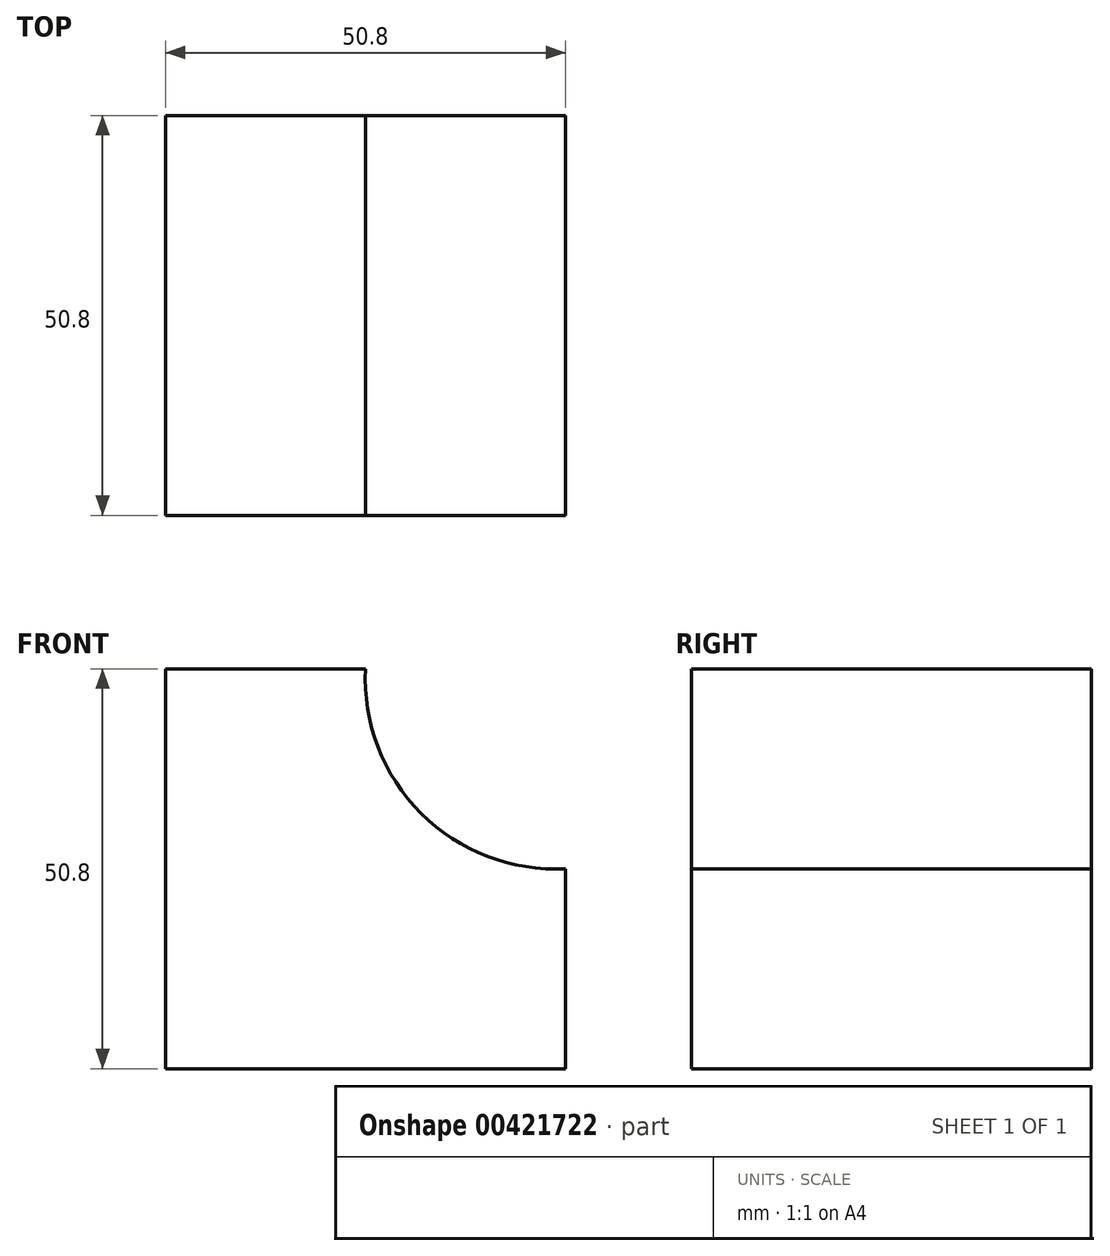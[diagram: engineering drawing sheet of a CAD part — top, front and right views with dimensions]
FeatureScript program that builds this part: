
annotation { "Feature Type Name" : "Feature", "Feature Type Description" : "" }
export const myFeature = defineFeature(function(context is Context, id is Id, definition is map)
    precondition{}
    {
        {
            var Q0;
            Q0=qCreatedBy(makeId("Front.planeOp"),FACE);
            var sketch = newSketch(context, id + "F0", { "sketchPlane" : qUnion([Q0])});
            skLineSegment(sketch, "E0", {"start": v(0, 0) * mm, "end": v(-50.8, 0) * mm});
            skLineSegment(sketch, "E1", {"start": v(-50.8, 0) * mm, "end": v(-50.8, 50.8) * mm});
            skLineSegment(sketch, "E2", {"start": v(-50.8, 50.8) * mm, "end": v(-25.4, 50.8) * mm});
            skLineSegment(sketch, "E3", {"start": v(0, 0) * mm, "end": v(0, 25.4) * mm});
            skArc(sketch, "E4", {"start": v(-25.4, 50.8) * mm, "mid": v(-18.36, 32.44) * mm, "end": v(0, 25.4) * mm});
            skSolve(sketch);
        }
        {
            var Q0;
            Q0=makeQuery(id+"F0.imprint","IMPRINT",FACE,{"disambiguationData":[TD([[makeQuery(id+"F0.imprint","IMPRINT",EDGE,{"derivedFrom":sQuery(id+"F0.wireOp",EDGE,"E0")}),-1.0]])]});
            extrude(context, id + "F1", {"entities" : qUnion([Q0]), "depth" : 50.8 * mm});
        }
    });
